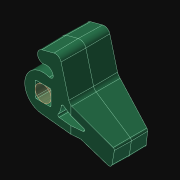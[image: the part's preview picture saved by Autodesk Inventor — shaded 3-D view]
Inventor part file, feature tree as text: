
AUTODESK INVENTOR PART (.ipt)
format: ipt  version: 2021.3 (Build 253353010, 353A)  size: 235,520 bytes
history: native  units: in
note: dims shown in document units (in); Inventor stores cm internally (conversion verified against a paired STEP export)
features: imported_body x2, sketch x1, other x1, extrude x1
ambient origin geometry x8: Origin, YZ Plane, XZ Plane, XY Plane, X Axis, Y Axis, Z Axis, Center Point
bodies: Body1 (feature_tree), Body2 (feature_tree)
feature tree (5):
  imported_body  "Imported1"
  imported_body  "Base1"
  sketch  "Sketch1"  dims[d0=1.0in d1=0.0in]
  other  "Srf1"
  extrude  "ExtrusionSrf1"  [1 undecoded]
note: 1 required parameter value undecoded (feature->parameter linkage not recoverable at this tier; creation-order binding heuristic only, values carry confidence <= 0.55)
